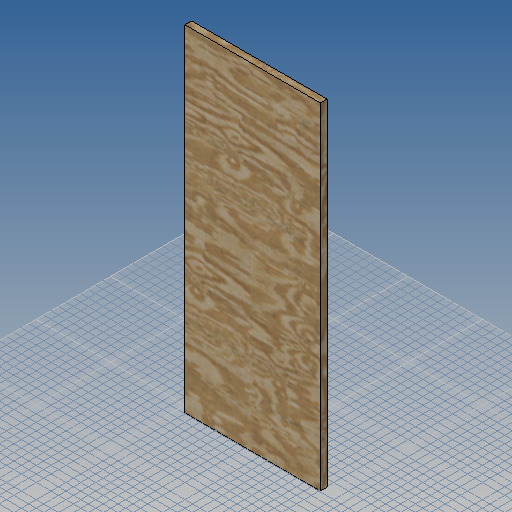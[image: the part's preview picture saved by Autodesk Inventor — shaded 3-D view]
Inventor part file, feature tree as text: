
AUTODESK INVENTOR PART (.ipt)
format: ipt  version: 2019 (Build 230136000, 136)  size: 239,616 bytes
history: native  units: mm
features: other x1, extrude x1, sketch x1
ambient origin geometry x8: Origin, YZ Plane, XZ Plane, XY Plane, X Axis, Y Axis, Z Axis, Center Point
bodies: Volumenkörper1 (feature_tree)
feature tree (3):
  other  "<userpath>\OneDrive\Dokumente\Inventor\Absauganlage\Absauganlage_Params.xlsx"
  extrude  "Extrusion1"  Depth=364.0mm
  sketch  "Skizze1"  dims[d0=904.0mm d1=364.0mm d2=18.0mm d3=0.0mm]
